# Revit family: RA 17 DIXIT LED OSCILLANTE
name_source: partatom
category: Lighting Fixtures
units: mm (PartAtom-declared; Revit-internal decimal feet)

## family parameters
Always vertical = Yes
Cut with Voids When Loaded = No
Host = Ceiling
Light Source = No
OmniClass Number = 23.80.70.11
OmniClass Title = Luminaries for Internal Lighting
Part Type = Normal
Room Calculation Point = No
Round Connector Dimension = Use Diameter
Shared = No

## types (1)
- RA 17 Dixit LED oscillante 33W 3000K
    Beam angle (°) = 0
    Body angle = 20.00°
    Body material = White Powder Coated Aluminium
    Default Elevation = 0 mm
    Description = Incasso professionale orientabile in grado di offrire elevate prestazioni illuminotecniche grazie all’utilizzo di sorgenti LED COB di ultima generazione.  
RA 17 DIXIT LED oscillante, a dissipazione termica passiva, garantisce un’alta densità luminosa ed eccellente resa cromatica. E’ facilmente installabile in controsoffitti da 1 a 30 mm anche a doghe. 
Orientamento: 40°+40° sull'asse orizzontale. 
I driver sono da ordinare separatamente, la potenza dell’apparecchio varia a seconda del driver scelto.
    Glass material = Glass
    Larghezza = 168 mm
    Manufacturer = ARIA
    Model = 248-230BN-21
    Type = RA 17 boby : RA 17 DIXIT LED OSCILLANTE 4250lm 33W 3000K CRI85-17° WHITE
    Type Comments = Ceiling recessed light
    Type Image = RA17DIXIT_LED_ADJ_TAB-Sito-Ivela.jpg
    URL = https://www.aria.lighting

## geometry (parser evidence)
native form markers: Sweep x6
no freeform markers — native parametric forms only
